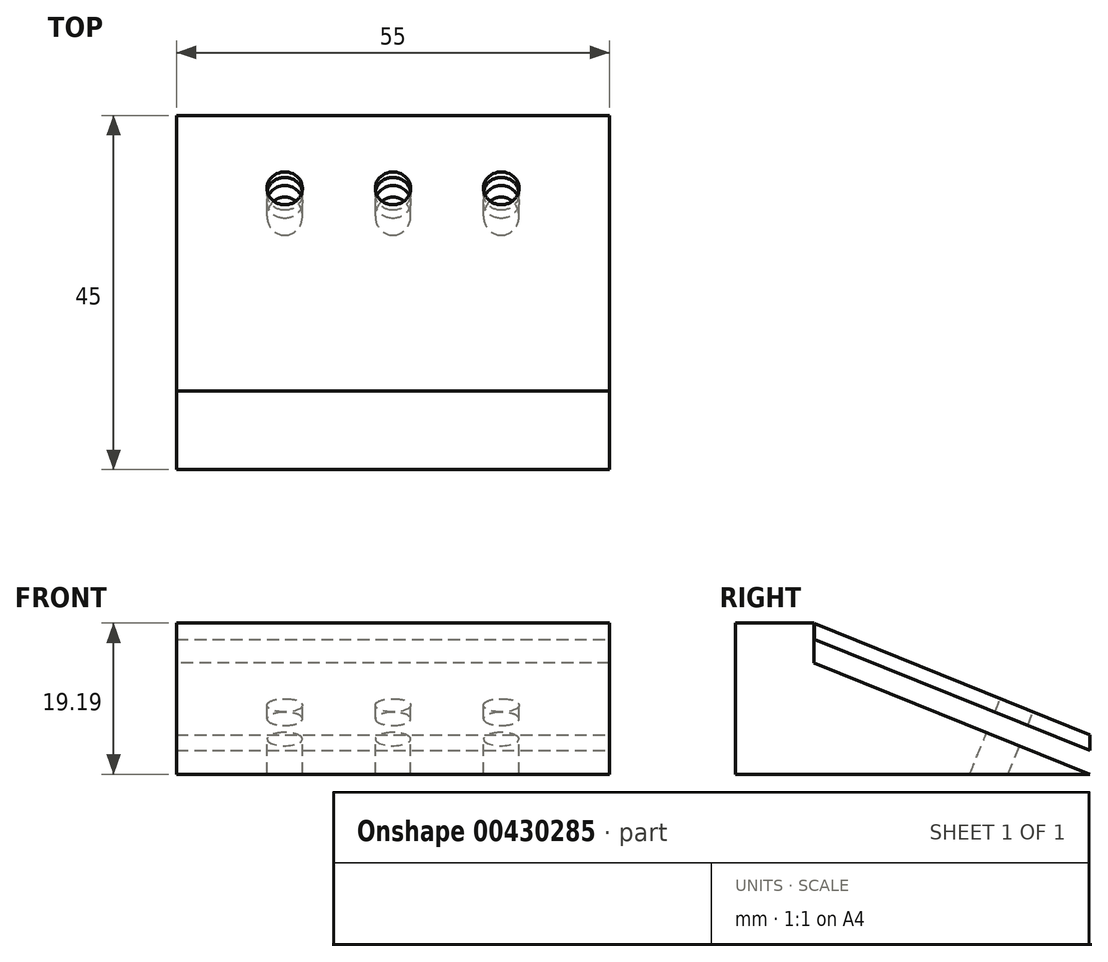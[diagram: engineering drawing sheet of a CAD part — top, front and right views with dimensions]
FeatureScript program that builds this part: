
annotation { "Feature Type Name" : "Feature", "Feature Type Description" : "" }
export const myFeature = defineFeature(function(context is Context, id is Id, definition is map)
    precondition{}
    {
        {
            var Q0;
            Q0=qCreatedBy(makeId("Right.planeOp"),FACE);
            var sketch = newSketch(context, id + "F0", { "sketchPlane" : qUnion([Q0])});
            skLineSegment(sketch, "E0", {"start": v(-10.02, 14.14) * mm, "end": v(-10.02, 0) * mm});
            skLineSegment(sketch, "E1", {"start": v(-10.02, 0) * mm, "end": v(24.98, 0) * mm});
            skLineSegment(sketch, "E2", {"start": v(24.98, 0) * mm, "end": v(-10.02, 14.14) * mm});
            skSolve(sketch);
        }
        {
            var Q0;
            Q0=makeQuery(id+"F0.imprint","IMPRINT",FACE,{"disambiguationData":[TD([[makeQuery(id+"F0.imprint","IMPRINT",EDGE,{"derivedFrom":sQuery(id+"F0.wireOp",EDGE,"E0")}),1.0]])]});
            extrude(context, id + "F1", {"entities" : qUnion([Q0]), "depth" : 55 * mm});
        }
        {
            var Q0;
            Q0=makeQuery(id+"F1.opExtrude","SWEPT_FACE",FACE,{"disambiguationData":[OSD([sQuery(id+"F0.wireOp",EDGE,"E0")])]});
            var sketch = newSketch(context, id + "F2", { "sketchPlane" : qUnion([Q0])});
            skLineSegment(sketch, "E3", {"start": v(55, 0) * mm, "end": v(55, 14.14) * mm});
            skLineSegment(sketch, "E4", {"start": v(0, 0) * mm, "end": v(0, 17.14) * mm});
            skLineSegment(sketch, "E5", {"start": v(55, 0) * mm, "end": v(55, 17.14) * mm});
            skLineSegment(sketch, "E6", {"start": v(0, 17.14) * mm, "end": v(55, 17.14) * mm});
            skLineSegment(sketch, "E7", {"start": v(-1049.54, 20.56) * mm, "end": v(-1049.54, 23.56) * mm});
            skSolve(sketch);
        }
        {
            var Q0;
            Q0=makeQuery(id+"F1.opExtrude","CAP_FACE",FACE,{"disambiguationData":[OSD([sQuery(id+"F0.wireOp",EDGE,"E0"),sQuery(id+"F0.wireOp",EDGE,"E1"),sQuery(id+"F0.wireOp",EDGE,"E2")])],"isStart":false});
            var sketch = newSketch(context, id + "F3", { "sketchPlane" : qUnion([Q0])});
            skLineSegment(sketch, "E8", {"start": v(24.98, 0) * mm, "end": v(24.98, 3) * mm});
            skSolve(sketch);
        }
        {
            var Q0;
            Q0=makeQuery(id+"F3.imprint","IMPRINT",FACE,{"disambiguationData":[TD([[makeQuery(id+"F3.imprint","IMPRINT",EDGE,{"derivedFrom":makeQuery(id+"F1.opExtrude","CAP_EDGE",EDGE,{"disambiguationData":[OSD([sQuery(id+"F0.wireOp",EDGE,"E0")])],"isStart":false})}),1.0]])]});
            var sketch = newSketch(context, id + "F4", { "sketchPlane" : qUnion([Q0])});
            skLineSegment(sketch, "E9", {"start": v(-10.02, 17.14) * mm, "end": v(24.98, 3) * mm});
            skLineSegment(sketch, "E10", {"start": v(-10.02, 17.14) * mm, "end": v(-10.02, 19.14) * mm});
            skLineSegment(sketch, "E11", {"start": v(24.98, 3) * mm, "end": v(24.98, 5) * mm});
            skLineSegment(sketch, "E12", {"start": v(-10.02, 19.14) * mm, "end": v(24.98, 5) * mm});
            skSolve(sketch);
        }
        {
            var Q0;
            Q0=makeQuery(id+"F4.imprint","IMPRINT",FACE,{"disambiguationData":[TD([[makeQuery(id+"F4.imprint","IMPRINT",EDGE,{"derivedFrom":sQuery(id+"F4.wireOp",EDGE,"E9")}),1.0]])]});
            extrude(context, id + "F5", {"entities" : qUnion([Q0]), "oppositeDirection" : true, "depth" : 55 * mm});
        }
        {
            var Q0;
            {var subQ1=sQuery(id+"F0.wireOp",EDGE,"E0");var subQ2=makeQuery(id+"F1.opExtrude","SWEPT_EDGE",EDGE,{"disambiguationData":[OSD([subQ1,sQuery(id+"F0.wireOp",EDGE,"E2")])]});Q0=makeQuery(id+"F2.imprint","IMPRINT",FACE,{"disambiguationData":[TD([[makeQuery(id+"F2.imprint","IMPRINT",EDGE,{"derivedFrom":subQ2}),1.0]])]});}
            var sketch = newSketch(context, id + "F6", { "sketchPlane" : qUnion([Q0])});
            skLineSegment(sketch, "E13", {"start": v(0, 0) * mm, "end": v(0, 19.2) * mm});
            skLineSegment(sketch, "E14", {"start": v(0, 19.2) * mm, "end": v(55, 19.2) * mm});
            skLineSegment(sketch, "E15", {"start": v(55, 19.2) * mm, "end": v(55, 0) * mm});
            skLineSegment(sketch, "E16", {"start": v(55, 0) * mm, "end": v(0, 0) * mm});
            skSolve(sketch);
        }
        {
            var Q0;
            Q0 = qSketchRegion(id + "F6", true);
            extrude(context, id + "F7", {"entities" : qUnion([Q0]), "operationType" : NewBodyOperationType.ADD, "depth" : 10 * mm});
        }
        {
            var Q0;
            Q0=makeQuery(id+"F5.opExtrude","SWEPT_FACE",FACE,{"disambiguationData":[OSD([sQuery(id+"F4.wireOp",EDGE,"E12")])]});
            var sketch = newSketch(context, id + "F8", { "sketchPlane" : qUnion([Q0])});
            skLineSegment(sketch, "E17", {"start": v(55, 21.3) * mm, "end": v(55, 11.3) * mm});
            skLineSegment(sketch, "E18", {"start": v(0, 11.3) * mm, "end": v(0, 21.3) * mm});
            skLineSegment(sketch, "E19", {"start": v(0, 21.3) * mm, "end": v(55, 21.3) * mm});
            skCircle(sketch, "E20", {"center": v(27.5, 11.3) * mm, "radius": 2.25 * mm});
            skLineSegment(sketch, "E21", {"start": v(27.5, 11.3) * mm, "end": v(13.75, 11.3) * mm});
            skCircle(sketch, "E22", {"center": v(13.75, 11.3) * mm, "radius": 2.25 * mm});
            skLineSegment(sketch, "E23", {"start": v(27.5, 11.3) * mm, "end": v(41.25, 11.3) * mm});
            skCircle(sketch, "E24", {"center": v(41.25, 11.3) * mm, "radius": 2.25 * mm});
            skSolve(sketch);
        }
        {
            var Q0;
            Q0=makeQuery(id+"F8.imprint","IMPRINT",FACE,{"disambiguationData":[TD([[makeQuery(id+"F8.imprint","IMPRINT",EDGE,{"derivedFrom":sQuery(id+"F8.wireOp",EDGE,"E22")}),1.0]])]});
            var Q1;
            {var subQ0=sQuery(id+"F8.wireOp",EDGE,"E21");var subQ1=sQuery(id+"F8.wireOp",EDGE,"E20");var subQ2=makeQuery(id+"F8.imprint","INTERSECT",VERTEX,{"derivedFrom":[subQ1,subQ0]});Q1=makeQuery(id+"F8.imprint","IMPRINT",FACE,{"disambiguationData":[TD([[makeQuery(id+"F8.imprint","IMPRINT",EDGE,{"disambiguationData":[TD([[subQ2,-1.0]])],"derivedFrom":subQ1}),1.0]])]});}
            var Q2;
            {var subQ0=sQuery(id+"F8.wireOp",EDGE,"E21");var subQ1=sQuery(id+"F8.wireOp",EDGE,"E20");var subQ2=makeQuery(id+"F8.imprint","INTERSECT",VERTEX,{"derivedFrom":[subQ1,subQ0]});Q2=makeQuery(id+"F8.imprint","IMPRINT",FACE,{"disambiguationData":[TD([[makeQuery(id+"F8.imprint","IMPRINT",EDGE,{"disambiguationData":[TD([[subQ2,1.0]])],"derivedFrom":subQ1}),1.0]])]});}
            var Q3;
            Q3=makeQuery(id+"F8.imprint","IMPRINT",FACE,{"disambiguationData":[TD([[makeQuery(id+"F8.imprint","IMPRINT",EDGE,{"derivedFrom":sQuery(id+"F8.wireOp",EDGE,"E24")}),1.0]])]});
            extrude(context, id + "F9", {"entities" : qUnion([Q0, Q1, Q2, Q3]), "operationType" : NewBodyOperationType.REMOVE, "oppositeDirection" : true, "depth" : 25 * mm});
        }
    });
